# Revit family: 25. Plumbing_Fixtures_Grohe_Euphoria_cube_27704000_14_METRIC
name_source: partatom
category: Plumbing Fixtures
revit_build: Autodesk Revit 2014 (Build: 20130308_1515(x64)
units: mm (PartAtom-declared; Revit-internal decimal feet)

## types (1)
- 25. Plumbing_Fixtures_Grohe_Euphoria_cube_27704000_14_METRIC
    ADA Compliant = Yes
    Assembly Code = C1030220
    AssetType = Fixed
    Base Material = Grohe-Chrome
    CW Connection = No
    CWFU = 0
    ClassificationName = Uniclass2015
    ClassificationValue = Pr_40_20_87_75
    Cold Water Connection Diameter = 10 mm  [stored 0.0328084 ft]
    Color = Chrome
    Cost = 0 $
    Default Elevation = 600 mm
    Description = Euphoria Cube Shower outlet elbow
    DocumentationMaintenance = https://specifi.bimstore.co.uk
    DocumentationTechnical = https://specifi.bimstore.co.uk
    DurationUnit = Years
    Ecojoy = No
    ExpectedLife = 0
    Finish = Chrome
    HW Connection = No
    HWFU = 0
    Height = 210 mm  [stored 0.688976 ft]
    Hot Water Connection Diameter = 10 mm  [stored 0.0328084 ft]
    Keynote = N13
    Length = 52 mm
    Low Emitting Material = No
    Manufacturer = Grohe AG
    Material = Chrome
    Model = Euphoria Cube - 27704000
    ModelNumber = 27704000
    NBSDescription = Shower fittings package
    NBSObjectName = Shower fittings package
    NBSReference = 45-35-70/330
    Name = Euphoria Cube - 27704000
    Percentage of Recycled Content = 0
    Plate Width = 52 mm
    Product Page URL = http://www.grohe.co.uk
    ProductionYear = 2015
    Spare Parts List = http://www.grohe.co.uk
    Type Comments = Euphoria Cube Shower outlet elbow
    TypeName = Euphoria Cube Shower outlet elbow
    URL = www.grohe.com
    Vent Connection = No
    WFU = 0
    WarrantyDurationUnit = Years
    Waste Connection = No
    Width = 100 mm  [stored 0.328084 ft]
    _BIMspec_GUID = 0
    _current revision = 1
    _distributed by = www.bimstore.co.uk

note: [stored X ft] marks values corroborated as IEEE doubles in the binary element streams (Revit-internal decimal feet)

## geometry (parser evidence)
native form markers: Blend x12, Sweep x1
no freeform markers — native parametric forms only
